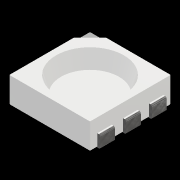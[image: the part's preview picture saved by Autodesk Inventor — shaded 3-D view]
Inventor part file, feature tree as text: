
AUTODESK INVENTOR PART (.ipt)
format: ipt  version: 2017 SP1 (Build 210196100, 196)  size: 265,728 bytes
history: native  units: mm
features: projected_geometry x8, sketch x5, extrude x4, other x2, fillet x2, pattern_linear x1, revolve x1
ambient origin geometry x8: Origin, YZ Plane, XZ Plane, XY Plane, X Axis, Y Axis, Z Axis, Center Point
bodies: Body1 (feature_tree)
feature tree (23):
  other  "Твердое тело1"
  extrude  "Выдавливание1"  Depth=1.0mm
  pattern_linear  "Прямоуг.массив1"  Spacing1=0.9mm  [1 undecoded]
  extrude  "Выдавливание2"  Depth=0.02mm TaperAngle=0.0deg
  extrude  "Выдавливание3"  Depth=1.6mm
  fillet  "Сопряжение1"  Radius=4.4mm
  fillet  "Сопряжение2"  Radius=5.4mm
  extrude  "Выдавливание4"  Depth=5.0mm
  other  "РабПлоскость1"
  revolve  "Вращение1"
  sketch  "Эскиз1"
  sketch  "Эскиз2"
  projected_geometry  "Спроецированная петля1"
  projected_geometry  "Спроецированная петля2"
  sketch  "Эскиз3"
  projected_geometry  "Спроецированная петля3"
  projected_geometry  "Спроецированная петля4"
  projected_geometry  "Спроецированная петля5"
  projected_geometry  "Спроецированная петля6"
  projected_geometry  "Спроецированная петля7"
  sketch  "Эскиз4"
  projected_geometry  "Спроецированная петля8"
  sketch  "Эскиз5"
note: 1 required parameter value undecoded (feature->parameter linkage not recoverable at this tier; creation-order binding heuristic only, values carry confidence <= 0.55)
